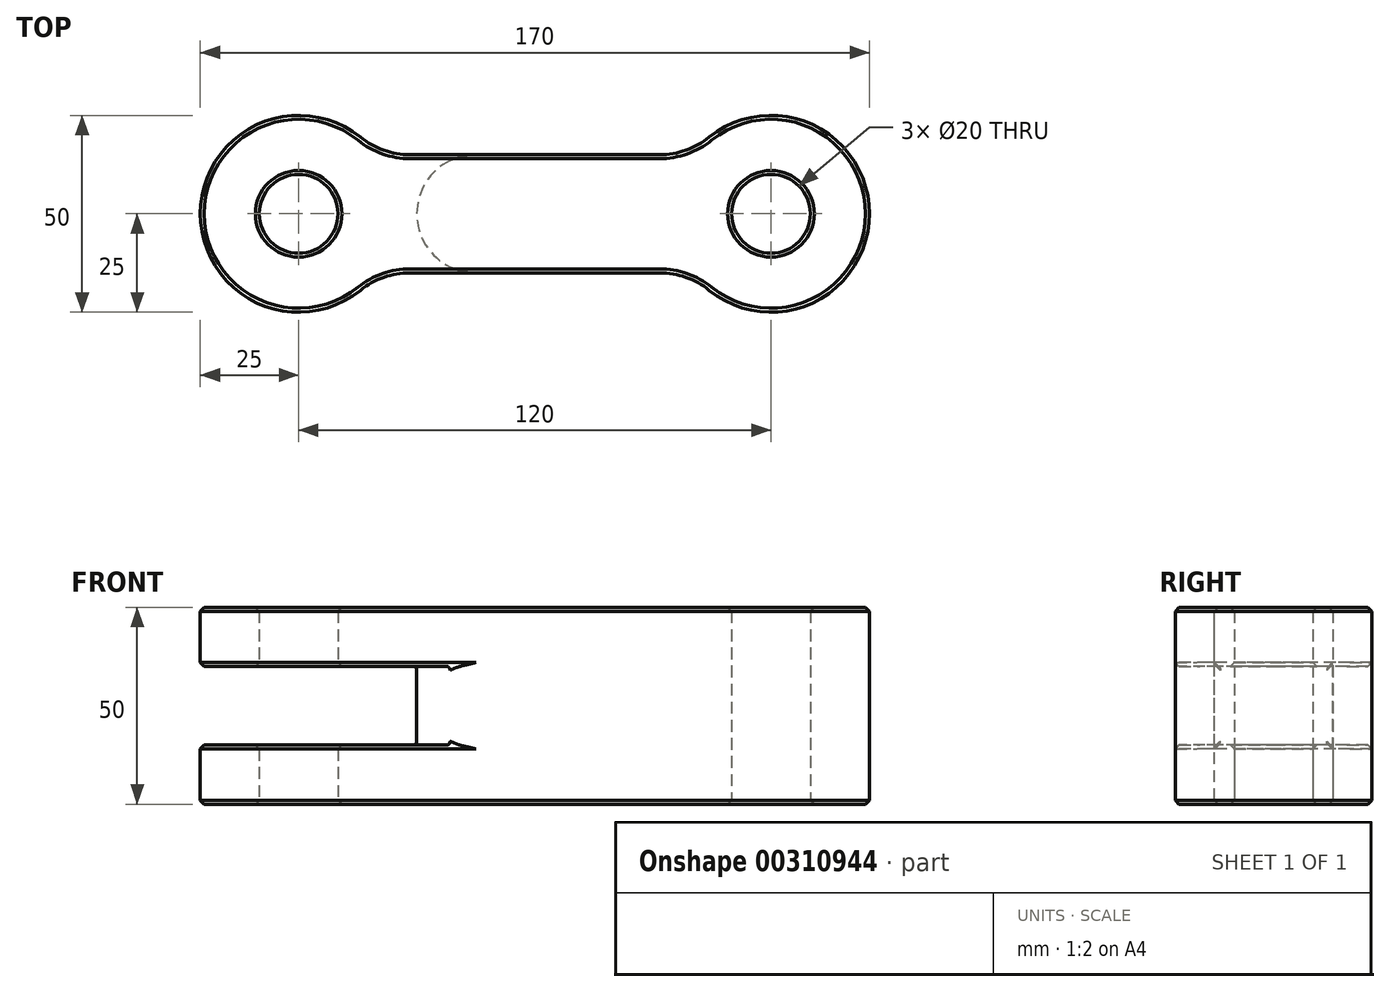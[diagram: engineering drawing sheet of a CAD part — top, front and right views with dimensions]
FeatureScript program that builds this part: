
annotation { "Feature Type Name" : "Feature", "Feature Type Description" : "" }
export const myFeature = defineFeature(function(context is Context, id is Id, definition is map)
    precondition{}
    {
        {
            var Q0;
            Q0=qCreatedBy(makeId("Top.planeOp"),FACE);
            var sketch = newSketch(context, id + "F0", { "sketchPlane" : qUnion([Q0])});
            skArc(sketch, "E0", {"start": v(-40, 15) * mm, "mid": v(-85, 0) * mm, "end": v(-40, -15) * mm});
            skLineSegment(sketch, "E1.bottom", {"start": v(-40, 15) * mm, "end": v(40, 15) * mm});
            skLineSegment(sketch, "E2.MirrorCS", {"start": v(-40, -15) * mm, "end": v(40, -15) * mm});
            skArc(sketch, "E3.MirrorCS", {"start": v(40, 15) * mm, "mid": v(85, 0) * mm, "end": v(40, -15) * mm});
            skCircle(sketch, "E4", {"center": v(60, 0) * mm, "radius": 10 * mm});
            skCircle(sketch, "E5", {"center": v(-60, 0) * mm, "radius": 10 * mm});
            skSolve(sketch);
        }
        {
            var Q0;
            Q0=makeQuery(id+"F0.imprint","IMPRINT",FACE,{"disambiguationData":[TD([[makeQuery(id+"F0.imprint","IMPRINT",EDGE,{"derivedFrom":sQuery(id+"F0.wireOp",EDGE,"E0")}),1.0]])]});
            extrude(context, id + "F1", {"entities" : qUnion([Q0]), "depth" : 50 * mm, "symmetric" : true});
        }
        {
            var Q0;
            Q0=makeQuery(id+"F1.opExtrude","SWEPT_EDGE",EDGE,{"disambiguationData":[OSD([sQuery(id+"F0.wireOp",EDGE,"E0"),sQuery(id+"F0.wireOp",EDGE,"E2.MirrorCS")])]});
            var Q1;
            Q1=makeQuery(id+"F1.opExtrude","SWEPT_EDGE",EDGE,{"disambiguationData":[OSD([sQuery(id+"F0.wireOp",EDGE,"E2.MirrorCS"),sQuery(id+"F0.wireOp",EDGE,"E3.MirrorCS")])]});
            var Q2;
            Q2=makeQuery(id+"F1.opExtrude","SWEPT_EDGE",EDGE,{"disambiguationData":[OSD([sQuery(id+"F0.wireOp",EDGE,"E1.bottom"),sQuery(id+"F0.wireOp",EDGE,"E3.MirrorCS")])]});
            var Q3;
            Q3=makeQuery(id+"F1.opExtrude","SWEPT_EDGE",EDGE,{"disambiguationData":[OSD([sQuery(id+"F0.wireOp",EDGE,"E0"),sQuery(id+"F0.wireOp",EDGE,"E1.bottom")])]});
            fillet(context, id + "F2", {"entities" : qUnion([Q0, Q1, Q2, Q3]), "radius" : 20 * mm, "tangentPropagation" : true, "allowEdgeOverflow" : false});
        }
        {
            var Q0;
            Q0=qCreatedBy(makeId("Top.planeOp"),FACE);
            var sketch = newSketch(context, id + "F3", { "sketchPlane" : qUnion([Q0])});
            skLineSegment(sketch, "E6.bottom", {"start": v(-90, 30) * mm, "end": v(-30, 30) * mm});
            skLineSegment(sketch, "E6.top", {"start": v(-90, -30) * mm, "end": v(-30, -30) * mm});
            skLineSegment(sketch, "E6.left", {"start": v(-90, 30) * mm, "end": v(-90, -30) * mm});
            skLineSegment(sketch, "E6.right", {"start": v(-30, 30) * mm, "end": v(-30, -30) * mm});
            skSolve(sketch);
        }
        {
            var Q0;
            Q0=makeQuery(id+"F3.imprint","IMPRINT",FACE,{"disambiguationData":[TD([[makeQuery(id+"F3.imprint","IMPRINT",EDGE,{"derivedFrom":sQuery(id+"F3.wireOp",EDGE,"E6.bottom")}),-1.0]])]});
            extrude(context, id + "F4", {"entities" : qUnion([Q0]), "operationType" : NewBodyOperationType.REMOVE, "oppositeDirection" : true, "depth" : 20 * mm, "symmetric" : true});
        }
        {
            var Q0;
            Q0=makeQuery(id+"F1.opExtrude","CAP_FACE",FACE,{"disambiguationData":[OSD([sQuery(id+"F0.wireOp",EDGE,"E0"),sQuery(id+"F0.wireOp",EDGE,"E1.bottom"),sQuery(id+"F0.wireOp",EDGE,"E2.MirrorCS"),sQuery(id+"F0.wireOp",EDGE,"E3.MirrorCS")])],"isStart":false});
            var sketch = newSketch(context, id + "F5", { "sketchPlane" : qUnion([Q0])});
            skLineSegment(sketch, "E7.bottom", {"start": v(30, 30) * mm, "end": v(90, 30) * mm});
            skLineSegment(sketch, "E7.top", {"start": v(30, -30) * mm, "end": v(90, -30) * mm});
            skLineSegment(sketch, "E7.left", {"start": v(30, 30) * mm, "end": v(30, -30) * mm});
            skLineSegment(sketch, "E7.right", {"start": v(90, 30) * mm, "end": v(90, -30) * mm});
            skSolve(sketch);
        }
        {
            var Q0;
            {var subQ1=sQuery(id+"F0.wireOp",EDGE,"E3.MirrorCS");var subQ9=makeQuery(id+"F1.opExtrude","CAP_EDGE",EDGE,{"disambiguationData":[OSD([subQ1])],"isStart":false});Q0=makeQuery(id+"F5.imprint","IMPRINT",FACE,{"disambiguationData":[TD([[makeQuery(id+"F5.imprint","IMPRINT",EDGE,{"derivedFrom":subQ9}),-1.0]])]});}
            extrude(context, id + "F6", {"entities" : qUnion([Q0]), "operationType" : NewBodyOperationType.REMOVE, "oppositeDirection" : true, "depth" : 15 * mm});
        }
        {
            var Q0;
            Q0=makeQuery(id+"F4.boolean.opBoolean","INTERSECT",EDGE,{"derivedFrom":[makeQuery(id+"F1.opExtrude","SWEPT_FACE",FACE,{"disambiguationData":[OSD([sQuery(id+"F0.wireOp",EDGE,"E2.MirrorCS")])]}),makeQuery(id+"F4.opExtrude","SWEPT_FACE",FACE,{"disambiguationData":[OSD([sQuery(id+"F3.wireOp",EDGE,"E6.right")])]})]});
            var Q1;
            Q1=makeQuery(id+"F4.boolean.opBoolean","INTERSECT",EDGE,{"derivedFrom":[makeQuery(id+"F1.opExtrude","SWEPT_FACE",FACE,{"disambiguationData":[OSD([sQuery(id+"F0.wireOp",EDGE,"E1.bottom")])]}),makeQuery(id+"F4.opExtrude","SWEPT_FACE",FACE,{"disambiguationData":[OSD([sQuery(id+"F3.wireOp",EDGE,"E6.right")])]})]});
            var Q2;
            Q2=makeQuery(id+"F6.boolean.opBoolean","COPY",EDGE,{"derivedFrom":makeQuery(id+"F6.opExtrude","SWEPT_EDGE",EDGE,{"disambiguationData":[OSD([sQuery(id+"F0.wireOp",EDGE,"E1.bottom"),sQuery(id+"F5.wireOp",EDGE,"E7.left")])]})});
            var Q3;
            Q3=makeQuery(id+"FGRkAITluOdAFSo_1.1.F6.boolean.opBoolean","COPY",EDGE,{"derivedFrom":makeQuery(id+"FGRkAITluOdAFSo_1.1.F6.opExtrude","SWEPT_EDGE",EDGE,{"disambiguationData":[OSD([sQuery(id+"F0.wireOp",EDGE,"E1.bottom"),sQuery(id+"F5.wireOp",EDGE,"E7.left")])]})});
            var Q4;
            Q4=makeQuery(id+"FGRkAITluOdAFSo_1.1.F6.boolean.opBoolean","COPY",EDGE,{"derivedFrom":makeQuery(id+"FGRkAITluOdAFSo_1.1.F6.opExtrude","SWEPT_EDGE",EDGE,{"disambiguationData":[OSD([sQuery(id+"F0.wireOp",EDGE,"E2.MirrorCS"),sQuery(id+"F5.wireOp",EDGE,"E7.left")])]})});
            var Q5;
            Q5=makeQuery(id+"F6.boolean.opBoolean","COPY",EDGE,{"derivedFrom":makeQuery(id+"F6.opExtrude","SWEPT_EDGE",EDGE,{"disambiguationData":[OSD([sQuery(id+"F0.wireOp",EDGE,"E2.MirrorCS"),sQuery(id+"F5.wireOp",EDGE,"E7.left")])]})});
            fillet(context, id + "F7", {"entities" : qUnion([Q0, Q1, Q2, Q3, Q4, Q5]), "radius" : 15 * mm, "tangentPropagation" : true, "allowEdgeOverflow" : false});
        }
        {
            var Q0;
            {var subQ0=sQuery(id+"F0.wireOp",EDGE,"E5");Q0=makeQuery(id+"F4.boolean.opBoolean","SPLIT",FACE,{"disambiguationData":[TD([makeQuery(id+"F4.opExtrude","CAP_FACE",FACE,{"disambiguationData":[OSD([sQuery(id+"F3.wireOp",EDGE,"E6.bottom"),sQuery(id+"F3.wireOp",EDGE,"E6.top"),sQuery(id+"F3.wireOp",EDGE,"E6.left"),sQuery(id+"F3.wireOp",EDGE,"E6.right")])],"isStart":true})])],"derivedFrom":makeQuery(id+"F1.opExtrude","SWEPT_FACE",FACE,{"disambiguationData":[OSD([subQ0])]})});}
            var Q1;
            {var subQ0=sQuery(id+"F0.wireOp",EDGE,"E5");Q1=makeQuery(id+"F4.boolean.opBoolean","SPLIT",FACE,{"disambiguationData":[TD([makeQuery(id+"F4.opExtrude","CAP_FACE",FACE,{"disambiguationData":[OSD([sQuery(id+"F3.wireOp",EDGE,"E6.bottom"),sQuery(id+"F3.wireOp",EDGE,"E6.top"),sQuery(id+"F3.wireOp",EDGE,"E6.left"),sQuery(id+"F3.wireOp",EDGE,"E6.right")])],"isStart":false})])],"derivedFrom":makeQuery(id+"F1.opExtrude","SWEPT_FACE",FACE,{"disambiguationData":[OSD([subQ0])]})});}
            var Q2;
            Q2=makeQuery(id+"F1.opExtrude","SWEPT_FACE",FACE,{"disambiguationData":[OSD([sQuery(id+"F0.wireOp",EDGE,"E4")])]});
            var Q3;
            Q3=makeQuery(id+"FGRkAITluOdAFSo_1.1.F6.boolean.opBoolean","COPY",EDGE,{"derivedFrom":makeQuery(id+"FGRkAITluOdAFSo_1.1.F6.opExtrude","CAP_EDGE",EDGE,{"disambiguationData":[OSD([sQuery(id+"F0.wireOp",EDGE,"E3.MirrorCS")])],"isStart":false})});
            var Q4;
            Q4=makeQuery(id+"F6.boolean.opBoolean","COPY",EDGE,{"derivedFrom":makeQuery(id+"F6.opExtrude","CAP_EDGE",EDGE,{"disambiguationData":[OSD([sQuery(id+"F0.wireOp",EDGE,"E3.MirrorCS")])],"isStart":false})});
            var Q5;
            Q5=makeQuery(id+"F1.opExtrude","CAP_EDGE",EDGE,{"disambiguationData":[OSD([sQuery(id+"F0.wireOp",EDGE,"E0")])],"isStart":true});
            var Q6;
            Q6=makeQuery(id+"F4.boolean.opBoolean","INTERSECT",EDGE,{"derivedFrom":[makeQuery(id+"F1.opExtrude","SWEPT_FACE",FACE,{"disambiguationData":[OSD([sQuery(id+"F0.wireOp",EDGE,"E0")])]}),makeQuery(id+"F4.opExtrude","CAP_FACE",FACE,{"disambiguationData":[OSD([sQuery(id+"F3.wireOp",EDGE,"E6.bottom"),sQuery(id+"F3.wireOp",EDGE,"E6.top"),sQuery(id+"F3.wireOp",EDGE,"E6.left"),sQuery(id+"F3.wireOp",EDGE,"E6.right")])],"isStart":true})]});
            var Q7;
            Q7=makeQuery(id+"F4.boolean.opBoolean","INTERSECT",EDGE,{"derivedFrom":[makeQuery(id+"F1.opExtrude","SWEPT_FACE",FACE,{"disambiguationData":[OSD([sQuery(id+"F0.wireOp",EDGE,"E0")])]}),makeQuery(id+"F4.opExtrude","CAP_FACE",FACE,{"disambiguationData":[OSD([sQuery(id+"F3.wireOp",EDGE,"E6.bottom"),sQuery(id+"F3.wireOp",EDGE,"E6.top"),sQuery(id+"F3.wireOp",EDGE,"E6.left"),sQuery(id+"F3.wireOp",EDGE,"E6.right")])],"isStart":false})]});
            var Q8;
            Q8=makeQuery(id+"F1.opExtrude","CAP_EDGE",EDGE,{"disambiguationData":[OSD([sQuery(id+"F0.wireOp",EDGE,"E0")])],"isStart":false});
            chamfer(context, id + "F8", {"entities" : qUnion([Q0, Q1, Q2, Q3, Q4, Q5, Q6, Q7, Q8]), "width" : 1 * mm, "tangentPropagation" : true});
        }
        {
            var Q0;
            {var subQ0=sQuery(id+"F5.wireOp",EDGE,"E7.left");var subQ1=sQuery(id+"F0.wireOp",EDGE,"E1.bottom");Q0=makeQuery(id+"F7.opFillet","BLEND_EDGE",EDGE,{"blendedFrom":[makeQuery(id+"F6.boolean.opBoolean","COPY",EDGE,{"derivedFrom":makeQuery(id+"F6.opExtrude","SWEPT_EDGE",EDGE,{"disambiguationData":[OSD([subQ1,subQ0])]})}),makeQuery(id+"F6.boolean.opBoolean","COPY",FACE,{"derivedFrom":makeQuery(id+"F6.opExtrude","CAP_FACE",FACE,{"disambiguationData":[OSD([sQuery(id+"F0.wireOp",EDGE,"E0"),subQ1,sQuery(id+"F0.wireOp",EDGE,"E2.MirrorCS"),sQuery(id+"F0.wireOp",EDGE,"E3.MirrorCS"),sQuery(id+"F0.wireOp",EDGE,"E4"),sQuery(id+"F0.wireOp",EDGE,"E5"),subQ0])],"isStart":false})})],"blendedInto":[makeQuery(id+"F6.boolean.opBoolean","COPY",FACE,{"derivedFrom":makeQuery(id+"F6.opExtrude","CAP_FACE",FACE,{"disambiguationData":[OSD([sQuery(id+"F0.wireOp",EDGE,"E0"),subQ1,sQuery(id+"F0.wireOp",EDGE,"E2.MirrorCS"),sQuery(id+"F0.wireOp",EDGE,"E3.MirrorCS"),sQuery(id+"F0.wireOp",EDGE,"E4"),sQuery(id+"F0.wireOp",EDGE,"E5"),subQ0])],"isStart":false})})]});}
            var Q1;
            {var subQ0=sQuery(id+"F5.wireOp",EDGE,"E7.left");var subQ1=sQuery(id+"F0.wireOp",EDGE,"E2.MirrorCS");Q1=makeQuery(id+"F8.opChamfer","BLEND_EDGE",EDGE,{"blendedFrom":[makeQuery(id+"F6.boolean.opBoolean","COPY",EDGE,{"derivedFrom":makeQuery(id+"F6.opExtrude","CAP_EDGE",EDGE,{"disambiguationData":[OSD([subQ1])],"isStart":false})}),makeQuery(id+"F7.opFillet","BLEND_FACE",FACE,{"disambiguationData":[OSD([subQ1,subQ0]),TDD([makeQuery(id+"F6.boolean.opBoolean","COPY",EDGE,{"derivedFrom":makeQuery(id+"F6.opExtrude","SWEPT_EDGE",EDGE,{"disambiguationData":[OSD([subQ1,subQ0])]})})])]})],"blendedInto":[makeQuery(id+"F7.opFillet","BLEND_FACE",FACE,{"disambiguationData":[OSD([subQ1,subQ0]),TDD([makeQuery(id+"F6.boolean.opBoolean","COPY",EDGE,{"derivedFrom":makeQuery(id+"F6.opExtrude","SWEPT_EDGE",EDGE,{"disambiguationData":[OSD([subQ1,subQ0])]})})])]})]});}
            var Q2;
            {var subQ0=sQuery(id+"F5.wireOp",EDGE,"E7.left");var subQ1=sQuery(id+"F0.wireOp",EDGE,"E2.MirrorCS");Q2=makeQuery(id+"F8.opChamfer","BLEND_EDGE",EDGE,{"blendedFrom":[makeQuery(id+"F6.boolean.opBoolean","COPY",EDGE,{"derivedFrom":makeQuery(id+"F6.opExtrude","CAP_EDGE",EDGE,{"disambiguationData":[OSD([sQuery(id+"F0.wireOp",EDGE,"E1.bottom")])],"isStart":false})}),makeQuery(id+"F7.opFillet","BLEND_FACE",FACE,{"disambiguationData":[OSD([subQ1,subQ0]),TDD([makeQuery(id+"F6.boolean.opBoolean","COPY",EDGE,{"derivedFrom":makeQuery(id+"F6.opExtrude","SWEPT_EDGE",EDGE,{"disambiguationData":[OSD([subQ1,subQ0])]})})])]})],"blendedInto":[makeQuery(id+"F7.opFillet","BLEND_FACE",FACE,{"disambiguationData":[OSD([subQ1,subQ0]),TDD([makeQuery(id+"F6.boolean.opBoolean","COPY",EDGE,{"derivedFrom":makeQuery(id+"F6.opExtrude","SWEPT_EDGE",EDGE,{"disambiguationData":[OSD([subQ1,subQ0])]})})])]})]});}
            var Q3;
            {var subQ0=sQuery(id+"F5.wireOp",EDGE,"E7.left");var subQ1=sQuery(id+"F0.wireOp",EDGE,"E2.MirrorCS");Q3=makeQuery(id+"F8.opChamfer","BLEND_EDGE",EDGE,{"blendedFrom":[makeQuery(id+"FGRkAITluOdAFSo_1.1.F6.boolean.opBoolean","COPY",EDGE,{"derivedFrom":makeQuery(id+"FGRkAITluOdAFSo_1.1.F6.opExtrude","CAP_EDGE",EDGE,{"disambiguationData":[OSD([sQuery(id+"F0.wireOp",EDGE,"E1.bottom")])],"isStart":false})}),makeQuery(id+"F7.opFillet","BLEND_FACE",FACE,{"disambiguationData":[OSD([subQ1,subQ0]),TDD([makeQuery(id+"FGRkAITluOdAFSo_1.1.F6.boolean.opBoolean","COPY",EDGE,{"derivedFrom":makeQuery(id+"FGRkAITluOdAFSo_1.1.F6.opExtrude","SWEPT_EDGE",EDGE,{"disambiguationData":[OSD([subQ1,subQ0])]})})])]})],"blendedInto":[makeQuery(id+"F7.opFillet","BLEND_FACE",FACE,{"disambiguationData":[OSD([subQ1,subQ0]),TDD([makeQuery(id+"FGRkAITluOdAFSo_1.1.F6.boolean.opBoolean","COPY",EDGE,{"derivedFrom":makeQuery(id+"FGRkAITluOdAFSo_1.1.F6.opExtrude","SWEPT_EDGE",EDGE,{"disambiguationData":[OSD([subQ1,subQ0])]})})])]})]});}
            var Q4;
            {var subQ0=sQuery(id+"F5.wireOp",EDGE,"E7.left");var subQ1=sQuery(id+"F0.wireOp",EDGE,"E1.bottom");Q4=makeQuery(id+"F7.opFillet","BLEND_EDGE",EDGE,{"blendedFrom":[makeQuery(id+"FGRkAITluOdAFSo_1.1.F6.boolean.opBoolean","COPY",EDGE,{"derivedFrom":makeQuery(id+"FGRkAITluOdAFSo_1.1.F6.opExtrude","SWEPT_EDGE",EDGE,{"disambiguationData":[OSD([subQ1,subQ0])]})}),makeQuery(id+"FGRkAITluOdAFSo_1.1.F6.boolean.opBoolean","COPY",FACE,{"derivedFrom":makeQuery(id+"FGRkAITluOdAFSo_1.1.F6.opExtrude","CAP_FACE",FACE,{"disambiguationData":[OSD([sQuery(id+"F0.wireOp",EDGE,"E0"),subQ1,sQuery(id+"F0.wireOp",EDGE,"E2.MirrorCS"),sQuery(id+"F0.wireOp",EDGE,"E3.MirrorCS"),sQuery(id+"F0.wireOp",EDGE,"E4"),sQuery(id+"F0.wireOp",EDGE,"E5"),subQ0])],"isStart":false})})],"blendedInto":[makeQuery(id+"FGRkAITluOdAFSo_1.1.F6.boolean.opBoolean","COPY",FACE,{"derivedFrom":makeQuery(id+"FGRkAITluOdAFSo_1.1.F6.opExtrude","CAP_FACE",FACE,{"disambiguationData":[OSD([sQuery(id+"F0.wireOp",EDGE,"E0"),subQ1,sQuery(id+"F0.wireOp",EDGE,"E2.MirrorCS"),sQuery(id+"F0.wireOp",EDGE,"E3.MirrorCS"),sQuery(id+"F0.wireOp",EDGE,"E4"),sQuery(id+"F0.wireOp",EDGE,"E5"),subQ0])],"isStart":false})})]});}
            var Q5;
            {var subQ0=sQuery(id+"F5.wireOp",EDGE,"E7.left");var subQ1=sQuery(id+"F0.wireOp",EDGE,"E2.MirrorCS");Q5=makeQuery(id+"F8.opChamfer","BLEND_EDGE",EDGE,{"blendedFrom":[makeQuery(id+"FGRkAITluOdAFSo_1.1.F6.boolean.opBoolean","COPY",EDGE,{"derivedFrom":makeQuery(id+"FGRkAITluOdAFSo_1.1.F6.opExtrude","CAP_EDGE",EDGE,{"disambiguationData":[OSD([subQ1])],"isStart":false})}),makeQuery(id+"F7.opFillet","BLEND_FACE",FACE,{"disambiguationData":[OSD([subQ1,subQ0]),TDD([makeQuery(id+"FGRkAITluOdAFSo_1.1.F6.boolean.opBoolean","COPY",EDGE,{"derivedFrom":makeQuery(id+"FGRkAITluOdAFSo_1.1.F6.opExtrude","SWEPT_EDGE",EDGE,{"disambiguationData":[OSD([subQ1,subQ0])]})})])]})],"blendedInto":[makeQuery(id+"F7.opFillet","BLEND_FACE",FACE,{"disambiguationData":[OSD([subQ1,subQ0]),TDD([makeQuery(id+"FGRkAITluOdAFSo_1.1.F6.boolean.opBoolean","COPY",EDGE,{"derivedFrom":makeQuery(id+"FGRkAITluOdAFSo_1.1.F6.opExtrude","SWEPT_EDGE",EDGE,{"disambiguationData":[OSD([subQ1,subQ0])]})})])]})]});}
            var Q6;
            {var subQ0=sQuery(id+"F3.wireOp",EDGE,"E6.right");Q6=makeQuery(id+"F7.opFillet","BLEND_EDGE",EDGE,{"blendedFrom":[makeQuery(id+"F4.boolean.opBoolean","INTERSECT",EDGE,{"derivedFrom":[makeQuery(id+"F1.opExtrude","SWEPT_FACE",FACE,{"disambiguationData":[OSD([sQuery(id+"F0.wireOp",EDGE,"E1.bottom")])]}),makeQuery(id+"F4.opExtrude","SWEPT_FACE",FACE,{"disambiguationData":[OSD([subQ0])]})]}),makeQuery(id+"F4.boolean.opBoolean","COPY",FACE,{"derivedFrom":makeQuery(id+"F4.opExtrude","CAP_FACE",FACE,{"disambiguationData":[OSD([sQuery(id+"F3.wireOp",EDGE,"E6.bottom"),sQuery(id+"F3.wireOp",EDGE,"E6.top"),sQuery(id+"F3.wireOp",EDGE,"E6.left"),subQ0])],"isStart":false})})],"blendedInto":[makeQuery(id+"F4.boolean.opBoolean","COPY",FACE,{"derivedFrom":makeQuery(id+"F4.opExtrude","CAP_FACE",FACE,{"disambiguationData":[OSD([sQuery(id+"F3.wireOp",EDGE,"E6.bottom"),sQuery(id+"F3.wireOp",EDGE,"E6.top"),sQuery(id+"F3.wireOp",EDGE,"E6.left"),subQ0])],"isStart":false})})]});}
            var Q7;
            {var subQ0=sQuery(id+"F3.wireOp",EDGE,"E6.right");var subQ1=sQuery(id+"F0.wireOp",EDGE,"E2.MirrorCS");Q7=makeQuery(id+"F8.opChamfer","BLEND_EDGE",EDGE,{"blendedFrom":[makeQuery(id+"F4.boolean.opBoolean","INTERSECT",EDGE,{"derivedFrom":[makeQuery(id+"F1.opExtrude","SWEPT_FACE",FACE,{"disambiguationData":[OSD([subQ1])]}),makeQuery(id+"F4.opExtrude","CAP_FACE",FACE,{"disambiguationData":[OSD([sQuery(id+"F3.wireOp",EDGE,"E6.bottom"),sQuery(id+"F3.wireOp",EDGE,"E6.top"),sQuery(id+"F3.wireOp",EDGE,"E6.left"),subQ0])],"isStart":false})]}),makeQuery(id+"F7.opFillet","BLEND_FACE",FACE,{"disambiguationData":[OSD([subQ1,subQ0])]})],"blendedInto":[makeQuery(id+"F7.opFillet","BLEND_FACE",FACE,{"disambiguationData":[OSD([subQ1,subQ0])]})]});}
            var Q8;
            {var subQ0=sQuery(id+"F3.wireOp",EDGE,"E6.right");var subQ1=sQuery(id+"F0.wireOp",EDGE,"E2.MirrorCS");Q8=makeQuery(id+"F8.opChamfer","BLEND_EDGE",EDGE,{"blendedFrom":[makeQuery(id+"F4.boolean.opBoolean","INTERSECT",EDGE,{"derivedFrom":[makeQuery(id+"F1.opExtrude","SWEPT_FACE",FACE,{"disambiguationData":[OSD([subQ1])]}),makeQuery(id+"F4.opExtrude","CAP_FACE",FACE,{"disambiguationData":[OSD([sQuery(id+"F3.wireOp",EDGE,"E6.bottom"),sQuery(id+"F3.wireOp",EDGE,"E6.top"),sQuery(id+"F3.wireOp",EDGE,"E6.left"),subQ0])],"isStart":true})]}),makeQuery(id+"F7.opFillet","BLEND_FACE",FACE,{"disambiguationData":[OSD([subQ1,subQ0])]})],"blendedInto":[makeQuery(id+"F7.opFillet","BLEND_FACE",FACE,{"disambiguationData":[OSD([subQ1,subQ0])]})]});}
            var Q9;
            {var subQ0=sQuery(id+"F3.wireOp",EDGE,"E6.right");Q9=makeQuery(id+"F7.opFillet","BLEND_EDGE",EDGE,{"blendedFrom":[makeQuery(id+"F4.boolean.opBoolean","INTERSECT",EDGE,{"derivedFrom":[makeQuery(id+"F1.opExtrude","SWEPT_FACE",FACE,{"disambiguationData":[OSD([sQuery(id+"F0.wireOp",EDGE,"E1.bottom")])]}),makeQuery(id+"F4.opExtrude","SWEPT_FACE",FACE,{"disambiguationData":[OSD([subQ0])]})]}),makeQuery(id+"F4.boolean.opBoolean","COPY",FACE,{"derivedFrom":makeQuery(id+"F4.opExtrude","CAP_FACE",FACE,{"disambiguationData":[OSD([sQuery(id+"F3.wireOp",EDGE,"E6.bottom"),sQuery(id+"F3.wireOp",EDGE,"E6.top"),sQuery(id+"F3.wireOp",EDGE,"E6.left"),subQ0])],"isStart":true})})],"blendedInto":[makeQuery(id+"F4.boolean.opBoolean","COPY",FACE,{"derivedFrom":makeQuery(id+"F4.opExtrude","CAP_FACE",FACE,{"disambiguationData":[OSD([sQuery(id+"F3.wireOp",EDGE,"E6.bottom"),sQuery(id+"F3.wireOp",EDGE,"E6.top"),sQuery(id+"F3.wireOp",EDGE,"E6.left"),subQ0])],"isStart":true})})]});}
            var Q10;
            {var subQ0=sQuery(id+"F3.wireOp",EDGE,"E6.right");Q10=makeQuery(id+"F8.opChamfer","BLEND_EDGE",EDGE,{"blendedFrom":[makeQuery(id+"F4.boolean.opBoolean","INTERSECT",EDGE,{"derivedFrom":[makeQuery(id+"F1.opExtrude","SWEPT_FACE",FACE,{"disambiguationData":[OSD([sQuery(id+"F0.wireOp",EDGE,"E1.bottom")])]}),makeQuery(id+"F4.opExtrude","CAP_FACE",FACE,{"disambiguationData":[OSD([sQuery(id+"F3.wireOp",EDGE,"E6.bottom"),sQuery(id+"F3.wireOp",EDGE,"E6.top"),sQuery(id+"F3.wireOp",EDGE,"E6.left"),subQ0])],"isStart":true})]}),makeQuery(id+"F7.opFillet","BLEND_FACE",FACE,{"disambiguationData":[OSD([sQuery(id+"F0.wireOp",EDGE,"E2.MirrorCS"),subQ0])]})],"blendedInto":[makeQuery(id+"F7.opFillet","BLEND_FACE",FACE,{"disambiguationData":[OSD([sQuery(id+"F0.wireOp",EDGE,"E2.MirrorCS"),subQ0])]})]});}
            var Q11;
            {var subQ0=sQuery(id+"F3.wireOp",EDGE,"E6.right");Q11=makeQuery(id+"F8.opChamfer","BLEND_EDGE",EDGE,{"blendedFrom":[makeQuery(id+"F4.boolean.opBoolean","INTERSECT",EDGE,{"derivedFrom":[makeQuery(id+"F1.opExtrude","SWEPT_FACE",FACE,{"disambiguationData":[OSD([sQuery(id+"F0.wireOp",EDGE,"E1.bottom")])]}),makeQuery(id+"F4.opExtrude","CAP_FACE",FACE,{"disambiguationData":[OSD([sQuery(id+"F3.wireOp",EDGE,"E6.bottom"),sQuery(id+"F3.wireOp",EDGE,"E6.top"),sQuery(id+"F3.wireOp",EDGE,"E6.left"),subQ0])],"isStart":false})]}),makeQuery(id+"F7.opFillet","BLEND_FACE",FACE,{"disambiguationData":[OSD([sQuery(id+"F0.wireOp",EDGE,"E2.MirrorCS"),subQ0])]})],"blendedInto":[makeQuery(id+"F7.opFillet","BLEND_FACE",FACE,{"disambiguationData":[OSD([sQuery(id+"F0.wireOp",EDGE,"E2.MirrorCS"),subQ0])]})]});}
            fillet(context, id + "F9", {"entities" : qUnion([Q0, Q1, Q2, Q3, Q4, Q5, Q6, Q7, Q8, Q9, Q10, Q11]), "radius" : 1 * mm, "tangentPropagation" : true, "allowEdgeOverflow" : false});
        }
    });
